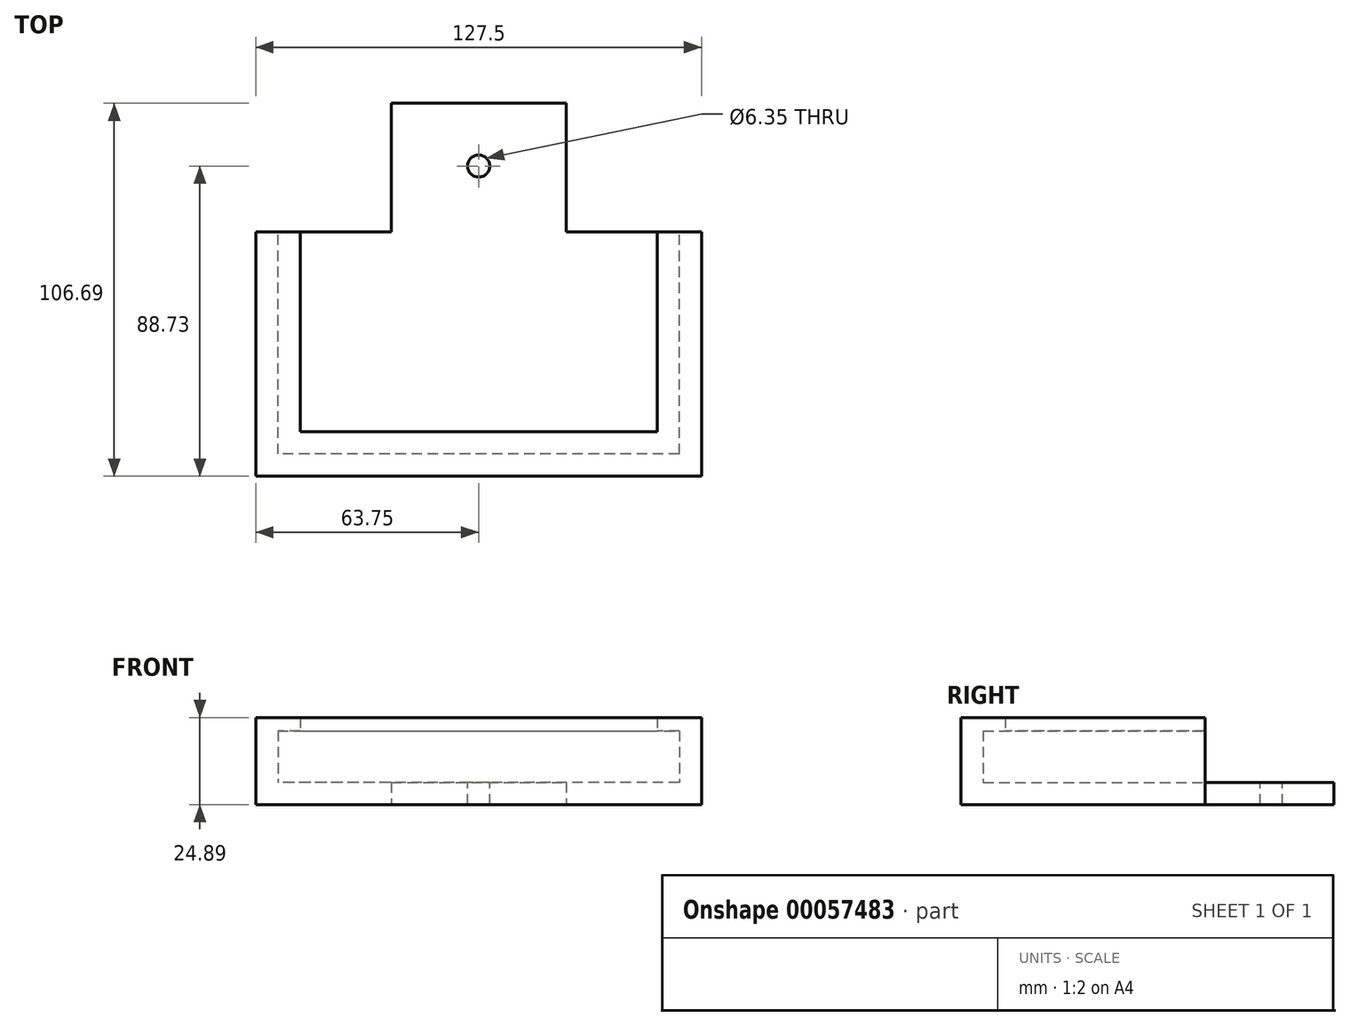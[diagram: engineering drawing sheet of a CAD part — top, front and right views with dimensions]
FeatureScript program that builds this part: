
annotation { "Feature Type Name" : "Feature", "Feature Type Description" : "" }
export const myFeature = defineFeature(function(context is Context, id is Id, definition is map)
    precondition{}
    {
        {
            var Q0;
            Q0=qCreatedBy(makeId("Top.planeOp"),FACE);
            var sketch = newSketch(context, id + "F0", { "sketchPlane" : qUnion([Q0])});
            skLineSegment(sketch, "E0.rect.bottom", {"start": v(57.4, -31.75) * mm, "end": v(-57.4, -31.75) * mm});
            skLineSegment(sketch, "E0.rect.top", {"start": v(57.4, 31.75) * mm, "end": v(-57.4, 31.75) * mm});
            skLineSegment(sketch, "E0.rect.left", {"start": v(57.4, -31.75) * mm, "end": v(57.4, 31.75) * mm});
            skLineSegment(sketch, "E0.rect.right", {"start": v(-57.4, -31.75) * mm, "end": v(-57.4, 31.75) * mm});
            skPoint(sketch, "E0.rect.middle", {"position": v(0, 0) * mm});
            skSolve(sketch);
        }
        {
            var Q0;
            Q0=makeQuery(id+"F0.imprint","IMPRINT",FACE,{"disambiguationData":[TD([[makeQuery(id+"F0.imprint","IMPRINT",EDGE,{"derivedFrom":sQuery(id+"F0.wireOp",EDGE,"E0.rect.bottom")}),-1.0]])]});
            extrude(context, id + "F1", {"entities" : qUnion([Q0]), "depth" : 6.35 * mm});
        }
        {
            var Q0;
            Q0=qCreatedBy(makeId("Top.planeOp"),FACE);
            var sketch = newSketch(context, id + "F2", { "sketchPlane" : qUnion([Q0])});
            skLineSegment(sketch, "E1.rect.bottom", {"start": v(-57.4, -31.75) * mm, "end": v(-63.75, -31.75) * mm});
            skLineSegment(sketch, "E1.rect.top", {"start": v(-57.4, 31.75) * mm, "end": v(-63.75, 31.75) * mm});
            skLineSegment(sketch, "E1.rect.left", {"start": v(-57.4, -31.75) * mm, "end": v(-57.4, 31.75) * mm});
            skLineSegment(sketch, "E1.rect.right", {"start": v(-63.75, -31.75) * mm, "end": v(-63.75, 31.75) * mm});
            skPoint(sketch, "E1.rect.middle", {"position": v(-60.58, 0) * mm});
            skSolve(sketch);
        }
        {
            var Q0;
            Q0=makeQuery(id+"F2.imprint","IMPRINT",FACE,{"disambiguationData":[TD([[makeQuery(id+"F2.imprint","IMPRINT",EDGE,{"derivedFrom":sQuery(id+"F2.wireOp",EDGE,"E1.rect.bottom")}),-1.0]])]});
            extrude(context, id + "F3", {"entities" : qUnion([Q0]), "operationType" : NewBodyOperationType.ADD, "depth" : 21.08 * mm});
        }
        {
            var Q0;
            Q0=qCreatedBy(makeId("Top.planeOp"),FACE);
            var sketch = newSketch(context, id + "F4", { "sketchPlane" : qUnion([Q0])});
            skLineSegment(sketch, "E2.bottom", {"start": v(-63.75, -31.75) * mm, "end": v(57.4, -31.75) * mm});
            skLineSegment(sketch, "E2.top", {"start": v(-63.75, -38.1) * mm, "end": v(57.4, -38.1) * mm});
            skLineSegment(sketch, "E2.left", {"start": v(-63.75, -31.75) * mm, "end": v(-63.75, -38.1) * mm});
            skLineSegment(sketch, "E2.right", {"start": v(57.4, -31.75) * mm, "end": v(57.4, -38.1) * mm});
            skSolve(sketch);
        }
        {
            var Q0;
            Q0=makeQuery(id+"F4.imprint","IMPRINT",FACE,{"disambiguationData":[TD([[makeQuery(id+"F4.imprint","IMPRINT",EDGE,{"derivedFrom":sQuery(id+"F4.wireOp",EDGE,"E2.bottom")}),-1.0]])]});
            extrude(context, id + "F5", {"entities" : qUnion([Q0]), "operationType" : NewBodyOperationType.ADD, "depth" : 21.08 * mm});
        }
        {
            var Q0;
            Q0=qCreatedBy(makeId("Top.planeOp"),FACE);
            var sketch = newSketch(context, id + "F6", { "sketchPlane" : qUnion([Q0])});
            skLineSegment(sketch, "E3.bottom", {"start": v(57.4, -38.1) * mm, "end": v(63.75, -38.1) * mm});
            skLineSegment(sketch, "E3.top", {"start": v(57.4, 31.75) * mm, "end": v(63.75, 31.75) * mm});
            skLineSegment(sketch, "E3.left", {"start": v(57.4, -38.1) * mm, "end": v(57.4, 31.75) * mm});
            skLineSegment(sketch, "E3.right", {"start": v(63.75, -38.1) * mm, "end": v(63.75, 31.75) * mm});
            skSolve(sketch);
        }
        {
            var Q0;
            Q0=makeQuery(id+"F6.imprint","IMPRINT",FACE,{"disambiguationData":[TD([[makeQuery(id+"F6.imprint","IMPRINT",EDGE,{"derivedFrom":sQuery(id+"F6.wireOp",EDGE,"E3.bottom")}),1.0]])]});
            extrude(context, id + "F7", {"entities" : qUnion([Q0]), "operationType" : NewBodyOperationType.ADD, "depth" : 21.08 * mm});
        }
        {
            var Q0;
            Q0=makeQuery(id+"F7.boolean.opBoolean","MERGE",FACE,{"derivedFrom":[makeQuery(id+"F5.boolean.opBoolean","MERGE",FACE,{"derivedFrom":[makeQuery(id+"F3.opExtrude","CAP_FACE",FACE,{"disambiguationData":[OSD([sQuery(id+"F2.wireOp",EDGE,"E1.rect.bottom"),sQuery(id+"F2.wireOp",EDGE,"E1.rect.top"),sQuery(id+"F2.wireOp",EDGE,"E1.rect.left"),sQuery(id+"F2.wireOp",EDGE,"E1.rect.right")])],"isStart":false}),makeQuery(id+"F5.opExtrude","CAP_FACE",FACE,{"disambiguationData":[OSD([sQuery(id+"F4.wireOp",EDGE,"E2.bottom"),sQuery(id+"F4.wireOp",EDGE,"E2.top"),sQuery(id+"F4.wireOp",EDGE,"E2.left"),sQuery(id+"F4.wireOp",EDGE,"E2.right")])],"isStart":false})]}),makeQuery(id+"F7.opExtrude","CAP_FACE",FACE,{"disambiguationData":[OSD([sQuery(id+"F6.wireOp",EDGE,"E3.bottom"),sQuery(id+"F6.wireOp",EDGE,"E3.top"),sQuery(id+"F6.wireOp",EDGE,"E3.left"),sQuery(id+"F6.wireOp",EDGE,"E3.right")])],"isStart":false})]});
            var sketch = newSketch(context, id + "F8", { "sketchPlane" : qUnion([Q0])});
            skLineSegment(sketch, "E4.bottom", {"start": v(63.75, 31.75) * mm, "end": v(51.05, 31.75) * mm});
            skLineSegment(sketch, "E4.top", {"start": v(63.75, -38.1) * mm, "end": v(51.05, -38.1) * mm});
            skLineSegment(sketch, "E4.left", {"start": v(63.75, 31.75) * mm, "end": v(63.75, -38.1) * mm});
            skLineSegment(sketch, "E4.right", {"start": v(51.05, 31.75) * mm, "end": v(51.05, -38.1) * mm});
            skSolve(sketch);
        }
        {
            var Q0;
            {var subQ1=makeQuery(id+"F7.opExtrude","CAP_EDGE",EDGE,{"disambiguationData":[OSD([sQuery(id+"F6.wireOp",EDGE,"E3.left")])],"isStart":false});Q0=makeQuery(id+"F8.imprint","IMPRINT",FACE,{"disambiguationData":[TD([[makeQuery(id+"F8.imprint","IMPRINT",EDGE,{"derivedFrom":subQ1}),1.0]])]});}
            var Q1;
            {var subQ1=sQuery(id+"F8.wireOp",EDGE,"E4.top");Q1=makeQuery(id+"F8.imprint","IMPRINT",FACE,{"disambiguationData":[TD([[makeQuery(id+"F8.imprint","IMPRINT",EDGE,{"derivedFrom":subQ1}),1.0]])]});}
            extrude(context, id + "F9", {"entities" : qUnion([Q0, Q1]), "operationType" : NewBodyOperationType.ADD, "depth" : 3.8 * mm});
        }
        {
            var Q0;
            Q0=makeQuery(id+"F7.boolean.opBoolean","MERGE",FACE,{"derivedFrom":[makeQuery(id+"F5.boolean.opBoolean","MERGE",FACE,{"derivedFrom":[makeQuery(id+"F3.opExtrude","CAP_FACE",FACE,{"disambiguationData":[OSD([sQuery(id+"F2.wireOp",EDGE,"E1.rect.bottom"),sQuery(id+"F2.wireOp",EDGE,"E1.rect.top"),sQuery(id+"F2.wireOp",EDGE,"E1.rect.left"),sQuery(id+"F2.wireOp",EDGE,"E1.rect.right")])],"isStart":false}),makeQuery(id+"F5.opExtrude","CAP_FACE",FACE,{"disambiguationData":[OSD([sQuery(id+"F4.wireOp",EDGE,"E2.bottom"),sQuery(id+"F4.wireOp",EDGE,"E2.top"),sQuery(id+"F4.wireOp",EDGE,"E2.left"),sQuery(id+"F4.wireOp",EDGE,"E2.right")])],"isStart":false})]}),makeQuery(id+"F7.opExtrude","CAP_FACE",FACE,{"disambiguationData":[OSD([sQuery(id+"F6.wireOp",EDGE,"E3.bottom"),sQuery(id+"F6.wireOp",EDGE,"E3.top"),sQuery(id+"F6.wireOp",EDGE,"E3.left"),sQuery(id+"F6.wireOp",EDGE,"E3.right")])],"isStart":false})]});
            var sketch = newSketch(context, id + "F10", { "sketchPlane" : qUnion([Q0])});
            skLineSegment(sketch, "E5.bottom", {"start": v(-63.75, -38.1) * mm, "end": v(51.05, -38.1) * mm});
            skLineSegment(sketch, "E5.top", {"start": v(-63.75, -25.4) * mm, "end": v(51.05, -25.4) * mm});
            skLineSegment(sketch, "E5.left", {"start": v(-63.75, -38.1) * mm, "end": v(-63.75, -25.4) * mm});
            skLineSegment(sketch, "E5.right", {"start": v(51.05, -38.1) * mm, "end": v(51.05, -25.4) * mm});
            skSolve(sketch);
        }
        {
            var Q0;
            {var subQ7=sQuery(id+"F10.wireOp",EDGE,"E5.bottom");Q0=makeQuery(id+"F10.imprint","IMPRINT",FACE,{"disambiguationData":[TD([[makeQuery(id+"F10.imprint","IMPRINT",EDGE,{"derivedFrom":subQ7}),1.0]])]});}
            var Q1;
            {var subQ0=sQuery(id+"F10.wireOp",EDGE,"E5.right");var subQ1=sQuery(id+"F10.wireOp",EDGE,"E5.top");var subQ2=makeQuery(id+"F10.imprint","INTERSECT",VERTEX,{"derivedFrom":[subQ1,subQ0]});Q1=makeQuery(id+"F10.imprint","IMPRINT",FACE,{"disambiguationData":[TD([[makeQuery(id+"F10.imprint","IMPRINT",EDGE,{"disambiguationData":[TD([[subQ2,1.0]])],"derivedFrom":subQ1}),-1.0]])]});}
            extrude(context, id + "F11", {"entities" : qUnion([Q0, Q1]), "operationType" : NewBodyOperationType.ADD, "depth" : 3.8 * mm});
        }
        {
            var Q0;
            Q0=makeQuery(id+"F7.boolean.opBoolean","MERGE",FACE,{"derivedFrom":[makeQuery(id+"F5.boolean.opBoolean","MERGE",FACE,{"derivedFrom":[makeQuery(id+"F3.opExtrude","CAP_FACE",FACE,{"disambiguationData":[OSD([sQuery(id+"F2.wireOp",EDGE,"E1.rect.bottom"),sQuery(id+"F2.wireOp",EDGE,"E1.rect.top"),sQuery(id+"F2.wireOp",EDGE,"E1.rect.left"),sQuery(id+"F2.wireOp",EDGE,"E1.rect.right")])],"isStart":false}),makeQuery(id+"F5.opExtrude","CAP_FACE",FACE,{"disambiguationData":[OSD([sQuery(id+"F4.wireOp",EDGE,"E2.bottom"),sQuery(id+"F4.wireOp",EDGE,"E2.top"),sQuery(id+"F4.wireOp",EDGE,"E2.left"),sQuery(id+"F4.wireOp",EDGE,"E2.right")])],"isStart":false})]}),makeQuery(id+"F7.opExtrude","CAP_FACE",FACE,{"disambiguationData":[OSD([sQuery(id+"F6.wireOp",EDGE,"E3.bottom"),sQuery(id+"F6.wireOp",EDGE,"E3.top"),sQuery(id+"F6.wireOp",EDGE,"E3.left"),sQuery(id+"F6.wireOp",EDGE,"E3.right")])],"isStart":false})]});
            var sketch = newSketch(context, id + "F12", { "sketchPlane" : qUnion([Q0])});
            skLineSegment(sketch, "E6.bottom", {"start": v(-63.75, 31.75) * mm, "end": v(-51.05, 31.75) * mm});
            skLineSegment(sketch, "E6.top", {"start": v(-63.75, -25.4) * mm, "end": v(-51.05, -25.4) * mm});
            skLineSegment(sketch, "E6.left", {"start": v(-63.75, 31.75) * mm, "end": v(-63.75, -25.4) * mm});
            skLineSegment(sketch, "E6.right", {"start": v(-51.05, 31.75) * mm, "end": v(-51.05, -25.4) * mm});
            skSolve(sketch);
        }
        {
            var Q0;
            {var subQ7=sQuery(id+"F12.wireOp",EDGE,"E6.left");Q0=makeQuery(id+"F12.imprint","IMPRINT",FACE,{"disambiguationData":[TD([[makeQuery(id+"F12.imprint","IMPRINT",EDGE,{"derivedFrom":subQ7}),-1.0]])]});}
            var Q1;
            {var subQ7=sQuery(id+"F12.wireOp",EDGE,"E6.right");Q1=makeQuery(id+"F12.imprint","IMPRINT",FACE,{"disambiguationData":[TD([[makeQuery(id+"F12.imprint","IMPRINT",EDGE,{"derivedFrom":subQ7}),-1.0]])]});}
            extrude(context, id + "F13", {"entities" : qUnion([Q0, Q1]), "operationType" : NewBodyOperationType.ADD, "depth" : 3.8 * mm});
        }
        {
            var Q0;
            Q0=qCreatedBy(makeId("Top.planeOp"),FACE);
            var sketch = newSketch(context, id + "F14", { "sketchPlane" : qUnion([Q0])});
            skLineSegment(sketch, "E7.rect.bottom", {"start": v(-25.02, -5) * mm, "end": v(25.02, -5) * mm});
            skLineSegment(sketch, "E7.rect.top", {"start": v(-25.02, 68.59) * mm, "end": v(25.02, 68.59) * mm});
            skLineSegment(sketch, "E7.rect.left", {"start": v(-25.02, -5) * mm, "end": v(-25.02, 68.59) * mm});
            skLineSegment(sketch, "E7.rect.right", {"start": v(25.02, -5) * mm, "end": v(25.02, 68.59) * mm});
            skPoint(sketch, "E7.rect.middle", {"position": v(0, 31.8) * mm});
            skSolve(sketch);
        }
        {
            var Q0;
            Q0=makeQuery(id+"F14.imprint","IMPRINT",FACE,{"disambiguationData":[TD([[makeQuery(id+"F14.imprint","IMPRINT",EDGE,{"derivedFrom":sQuery(id+"F14.wireOp",EDGE,"E7.rect.bottom")}),1.0]])]});
            extrude(context, id + "F15", {"entities" : qUnion([Q0]), "operationType" : NewBodyOperationType.ADD, "depth" : 6.35 * mm});
        }
        {
            var Q0;
            Q0=makeQuery(id+"F15.boolean.opBoolean","MERGE",FACE,{"derivedFrom":[makeQuery(id+"F1.opExtrude","CAP_FACE",FACE,{"disambiguationData":[OSD([sQuery(id+"F0.wireOp",EDGE,"E0.rect.bottom"),sQuery(id+"F0.wireOp",EDGE,"E0.rect.top"),sQuery(id+"F0.wireOp",EDGE,"E0.rect.left"),sQuery(id+"F0.wireOp",EDGE,"E0.rect.right")])],"isStart":false}),makeQuery(id+"F15.opExtrude","CAP_FACE",FACE,{"disambiguationData":[OSD([sQuery(id+"F14.wireOp",EDGE,"E7.rect.bottom"),sQuery(id+"F14.wireOp",EDGE,"E7.rect.top"),sQuery(id+"F14.wireOp",EDGE,"E7.rect.left"),sQuery(id+"F14.wireOp",EDGE,"E7.rect.right")])],"isStart":false})]});
            var sketch = newSketch(context, id + "F16", { "sketchPlane" : qUnion([Q0])});
            skCircle(sketch, "E8", {"center": v(0, 58.73) * mm, "radius": 2 * mm});
            skCircle(sketch, "E9", {"center": v(0, 50.63) * mm, "radius": 2.47 * mm});
            skCircle(sketch, "E10", {"center": v(0, 40.73) * mm, "radius": 2.42 * mm});
            skSolve(sketch);
        }
        {
            var Q0;
            Q0=sQuery(id+"F16.wireOp",VERTEX,"E9.center");
            var Q1;
            Q1=makeQuery(id+"F1.opExtrude","SWEPT_BODY",BODY,{"disambiguationData":[OSD([sQuery(id+"F0.wireOp",EDGE,"E0.rect.bottom"),sQuery(id+"F0.wireOp",EDGE,"E0.rect.top"),sQuery(id+"F0.wireOp",EDGE,"E0.rect.left"),sQuery(id+"F0.wireOp",EDGE,"E0.rect.right")])]});
            hole(context, id + "F17", {"style" : HoleStyle.SIMPLE, "holeDiameter" : 6.35 * mm, "endStyle" : HoleEndStyle.THROUGH, "locations" : qUnion([Q0]), "scope" : qUnion([Q1])});
        }
    });
